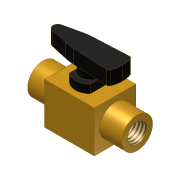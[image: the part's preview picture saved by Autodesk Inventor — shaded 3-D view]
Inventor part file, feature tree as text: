
AUTODESK INVENTOR PART (.ipt)
format: ipt  version: unknown  size: 252,928 bytes
history: native  units: mm (DEFAULTED — no unit token found)
features: extrude x10, sketch x10, projected_geometry x5, thread x2
ambient origin geometry x8: Origin, YZ Plane, XZ Plane, XY Plane, X Axis, Y Axis, Z Axis, Center Point
feature tree (27):
  extrude  "Extrusion1"  Depth=22.86mm
  extrude  "Extrusion2"  Depth=14.224mm
  extrude  "Extrusion3"  Depth=14.224mm
  extrude  "Extrusion4"  Depth=3.81mm TaperAngle=0.0deg
  extrude  "Extrusion5"  Depth=6.35mm TaperAngle=0.0deg
  extrude  "Extrusion6"  Depth=9.525mm TaperAngle=0.0deg
  extrude  "Extrusion7"  Depth=3.175mm
  extrude  "Extrusion9"  Depth=25.4mm TaperAngle=0.0deg
  thread  "Thread1"  [1 undecoded]
  thread  "Thread2"  [1 undecoded]
  extrude  "Extrusion10"  [1 undecoded]
  sketch  "Sketch1"  dims[d0=19.05mm d1=22.86mm]
  sketch  "Sketch2"  dims[d2=19.05mm d3=0.0mm d4=14.224mm]
  projected_geometry  "Projected Loop1"
  sketch  "Sketch3"  dims[d5=10.16mm d6=0.0mm d7=14.224mm]
  projected_geometry  "Projected Loop2"
  sketch  "Sketch4"  dims[d8=10.16mm d9=0.0mm d10=3.81mm d11=0.0mm]
  projected_geometry  "Projected Loop3"
  sketch  "Sketch5"  dims[d12=10.16mm d13=0.0mm d14=6.35mm d15=0.0mm]
  projected_geometry  "Projected Loop4"
  sketch  "Sketch6"  dims[d16=8.89mm d17=9.525mm d18=0.0mm]
  projected_geometry  "Projected Loop5"
  sketch  "Sketch7"  dims[d19=8.89mm d21=0.0mm d22=9.525mm d23=3.175mm]
  sketch  "Sketch8"  dims[d24=71.4502mm d25=0.0mm d26=25.4mm d27=0.0mm d28=25.4mm d29=0.0mm d30=1.6002mm d31=0.0mm]
  sketch  "Sketch9"
  sketch  "Sketch10"
  extrude  "Extrusion8"  [1 undecoded]
note: 4 required parameter values undecoded (feature->parameter linkage not recoverable at this tier; creation-order binding heuristic only, values carry confidence <= 0.55)
